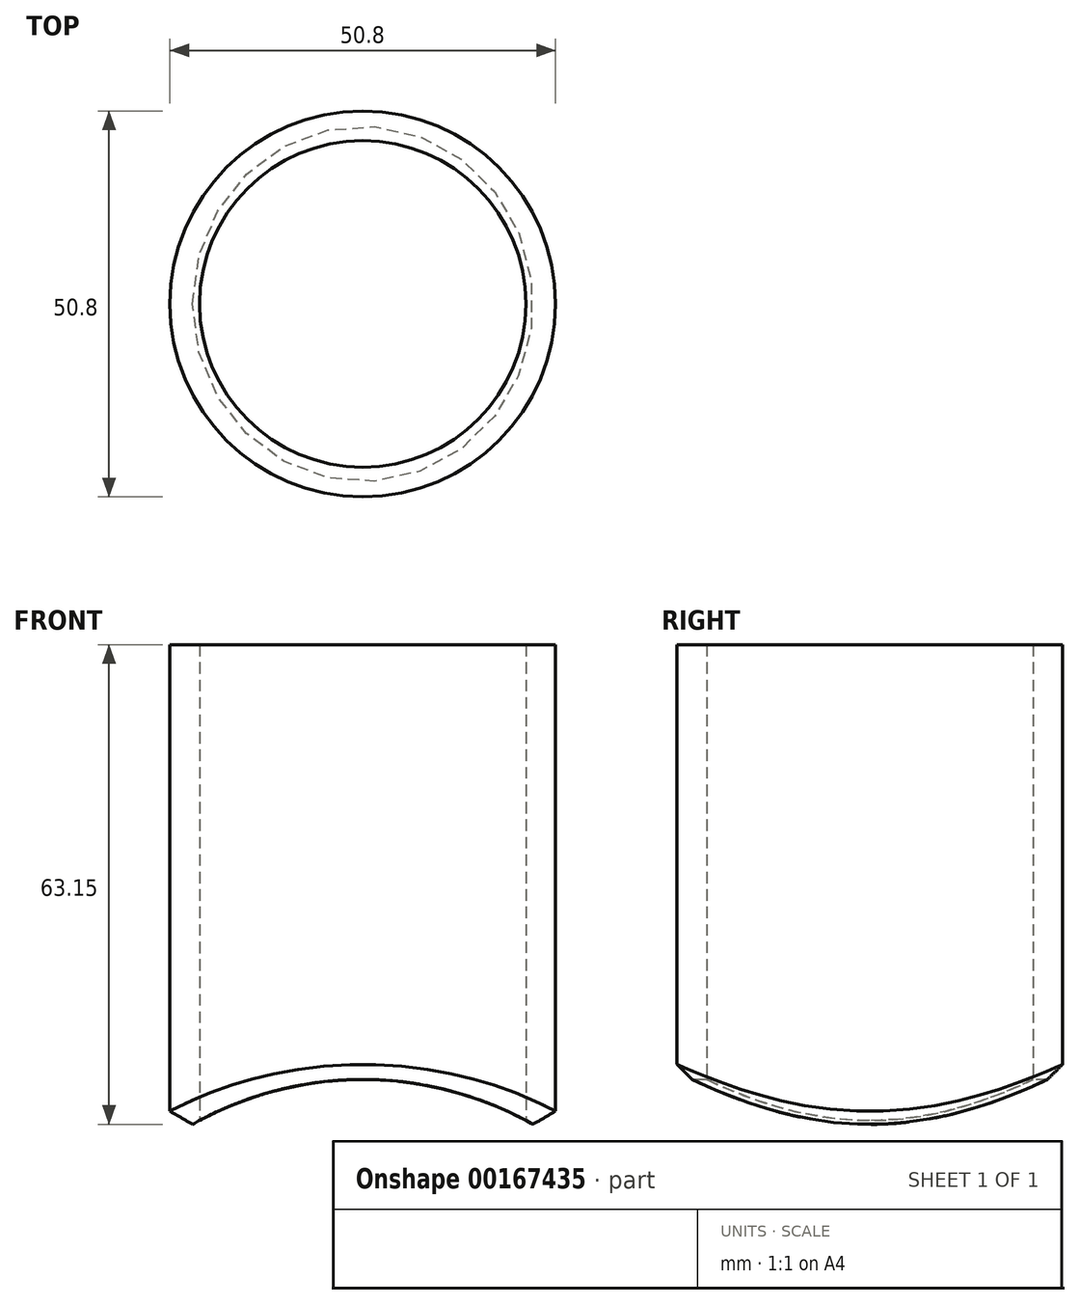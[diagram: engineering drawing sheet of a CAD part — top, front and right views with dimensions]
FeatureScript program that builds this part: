
annotation { "Feature Type Name" : "Feature", "Feature Type Description" : "" }
export const myFeature = defineFeature(function(context is Context, id is Id, definition is map)
    precondition{}
    {
        {
            var Q0;
            Q0=qCreatedBy(makeId("Top.planeOp"),FACE);
            var sketch = newSketch(context, id + "F0", { "sketchPlane" : qUnion([Q0])});
            skCircle(sketch, "E0", {"center": v(0, 0) * mm, "radius": 21.5 * mm});
            skCircle(sketch, "E1", {"center": v(0, 0) * mm, "radius": 25.4 * mm});
            skSolve(sketch);
        }
        {
            var Q0;
            Q0 = qSketchRegion(id + "F0", true);
            extrude(context, id + "F1", {"entities" : qUnion([Q0]), "depth" : 65 * mm});
        }
        {
            var Q0;
            Q0=qCreatedBy(makeId("Front.planeOp"),FACE);
            var sketch = newSketch(context, id + "F2", { "sketchPlane" : qUnion([Q0])});
            skCircle(sketch, "E2", {"center": v(0, -37.75) * mm, "radius": 45.5 * mm});
            skLineSegment(sketch, "E3", {"start": v(0, 0) * mm, "end": v(-25.4, 0) * mm});
            skSolve(sketch);
        }
        {
            var Q0;
            Q0 = qSketchRegion(id + "F2", true);
            extrude(context, id + "F3", {"entities" : qUnion([Q0]), "operationType" : NewBodyOperationType.REMOVE, "endBound" : BoundingType.SYMMETRIC, "oppositeDirection" : true, "depth" : 100 * mm});
        }
        {
            var Q0;
            Q0=makeQuery(id+"F3.boolean.opBoolean","INTERSECT",EDGE,{"derivedFrom":[makeQuery(id+"F1.opExtrude","SWEPT_FACE",FACE,{"disambiguationData":[OSD([sQuery(id+"F0.wireOp",EDGE,"E1")])]}),makeQuery(id+"F3.opExtrude","SWEPT_FACE",FACE,{"disambiguationData":[OSD([sQuery(id+"F2.wireOp",EDGE,"E2")])]})]});
            chamfer(context, id + "F4", {"entities" : qUnion([Q0]), "width" : 2 * mm, "tangentPropagation" : true});
        }
    });
